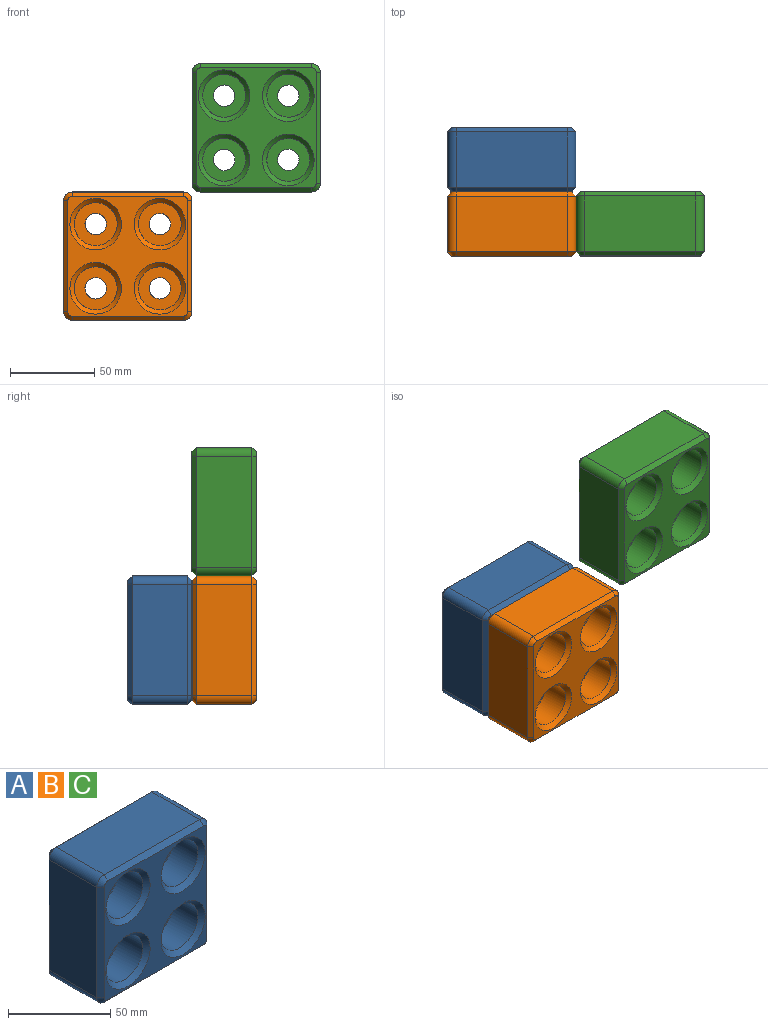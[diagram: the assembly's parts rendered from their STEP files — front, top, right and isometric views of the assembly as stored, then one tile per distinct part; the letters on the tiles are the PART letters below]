
ASSEMBLY  parts=3 mates=4
PART A: 42 faces, bbox 76.2x38.1x76.2 mm
  f0: cylinder r=6.35mm len=19.05mm, axis (0,1,0), area 760.1mm2, adj f9,f21
  f1: cylinder r=6.35mm len=19.05mm, axis (0,1,0), area 760.1mm2, adj f9,f19
  f2: cylinder r=6.35mm len=19.05mm, axis (0,1,0), area 760.1mm2, adj f9,f17
  f3: cylinder r=6.35mm len=19.05mm, axis (0,1,0), area 760.1mm2, adj f9,f15
  f4: plane 66.04x33.02mm, normal (-1,0,0), area 2180.6mm2, adj f10,f13,f25,f33
  f5: plane 66.04x33.02mm, normal (0,0,-1), area 2180.6mm2, adj f10,f11,f22,f30
  f6: plane 66.04x33.02mm, normal (1,0,0), area 2180.6mm2, adj f11,f12,f26,f34
  f7: plane 66.04x33.02mm, normal (0,0,1), area 2180.6mm2, adj f12,f13,f29,f37
  f8: plane 71.12x71.12mm, normal (0,-1,0), area 2114.7mm2, adj f22,f23,f24,f25,f26,f27,f28,f29
  f9: plane 71.12x71.12mm, normal (0,1,0), area 4545.8mm2, adj f0,f1,f2,f3,f30,f31,f32,f33
  f10: cylinder r=5.08mm len=33.02mm, axis (0,1,0), area 263.5mm2, adj f4,f5,f23,f31
  f11: cylinder r=5.08mm len=33.02mm, axis (0,-1,0), area 263.5mm2, adj f5,f6,f24,f32
  f12: cylinder r=5.08mm len=33.02mm, axis (0,1,0), area 263.5mm2, adj f6,f7,f28,f36
  f13: cylinder r=5.08mm len=33.02mm, axis (0,-1,0), area 263.5mm2, adj f4,f7,f27,f35
  f14: cylinder r=12.75mm len=25.5mm, axis (0,1,0), area 1322.6mm2, adj f15,f39
  f15: plane 25.5x25.5mm, normal (0,-1,0), area 384mm2, adj f3,f14
  f16: cylinder r=12.75mm len=25.5mm, axis (0,1,0), area 1322.6mm2, adj f17,f38
  f17: plane 25.5x25.5mm, normal (0,-1,0), area 384mm2, adj f2,f16
  f18: cylinder r=12.75mm len=25.5mm, axis (0,1,0), area 1322.6mm2, adj f19,f41
  f19: plane 25.5x25.5mm, normal (0,-1,0), area 384mm2, adj f1,f18
  f20: cylinder r=12.75mm len=25.5mm, axis (0,1,0), area 1322.6mm2, adj f21,f40
  f21: plane 25.5x25.5mm, normal (0,-1,0), area 384mm2, adj f0,f20
  f22: plane 66.04x2.54mm, normal (0,-0.71,-0.71), area 237.2mm2, adj f5,f8,f23,f24
  f23: cone r=2.54mm half-angle=45deg, axis (0,1,0), area 21.5mm2, adj f8,f10,f22,f25
  f24: cone r=2.54mm half-angle=45deg, axis (0,1,0), area 21.5mm2, adj f8,f11,f22,f26
  f25: plane 66.04x2.54mm, normal (-0.71,-0.71,0), area 237.2mm2, adj f4,f8,f23,f27
  f26: plane 66.04x2.54mm, normal (0.71,-0.71,0), area 237.2mm2, adj f6,f8,f24,f28
  f27: cone r=2.54mm half-angle=45deg, axis (0,1,0), area 21.5mm2, adj f8,f13,f25,f29
  f28: cone r=2.54mm half-angle=45deg, axis (0,1,0), area 21.5mm2, adj f8,f12,f26,f29
  f29: plane 66.04x2.54mm, normal (0,-0.71,0.71), area 237.2mm2, adj f7,f8,f27,f28
  f30: plane 66.04x2.54mm, normal (0,0.71,-0.71), area 237.2mm2, adj f5,f9,f31,f32
  f31: cone r=2.54mm half-angle=45deg, axis (0,-1,0), area 21.5mm2, adj f9,f10,f30,f33
  f32: cone r=2.54mm half-angle=45deg, axis (0,-1,0), area 21.5mm2, adj f9,f11,f30,f34
  f33: plane 66.04x2.54mm, normal (-0.71,0.71,0), area 237.2mm2, adj f4,f9,f31,f35
  f34: plane 66.04x2.54mm, normal (0.71,0.71,0), area 237.2mm2, adj f6,f9,f32,f36
  f35: cone r=2.54mm half-angle=45deg, axis (0,-1,0), area 21.5mm2, adj f9,f13,f33,f37
  f36: cone r=2.54mm half-angle=45deg, axis (0,-1,0), area 21.5mm2, adj f9,f12,f34,f37
  f37: plane 66.04x2.54mm, normal (0,0.71,0.71), area 237.2mm2, adj f7,f9,f35,f36
  f38: cone r=15.29mm half-angle=45deg, axis (0,-1,0), area 316.4mm2, adj f8,f16
  f39: cone r=15.29mm half-angle=45deg, axis (0,-1,0), area 316.4mm2, adj f8,f14
  f40: cone r=15.29mm half-angle=45deg, axis (0,-1,0), area 316.4mm2, adj f8,f20
  f41: cone r=15.29mm half-angle=45deg, axis (0,-1,0), area 316.4mm2, adj f8,f18
PART B: same geometry as A
PART C: same geometry as A
PLACE A rot(axis=(1,0,0),180deg) t=(16.81,48.17,0.55)mm
PLACE B t=(16.81,10.07,0.55)mm
PLACE C rot(axis=(0,1,0),90deg) t=(93.01,10.07,76.75)mm
MATE cylindrical A.f0 <-> B.f3  axis (0,-1,0) through (35.86,38.65,-18.5)mm
MATE planar C.f6 <-> B.f7  axis (0,0,-1) through (93.01,10.07,38.65)mm
MATE planar C.f5 <-> B.f6  axis (-1,0,0) through (54.91,10.07,76.75)mm
MATE planar A.f9 <-> B.f9  axis (0,-1,0) through (16.81,29.12,0.55)mm
